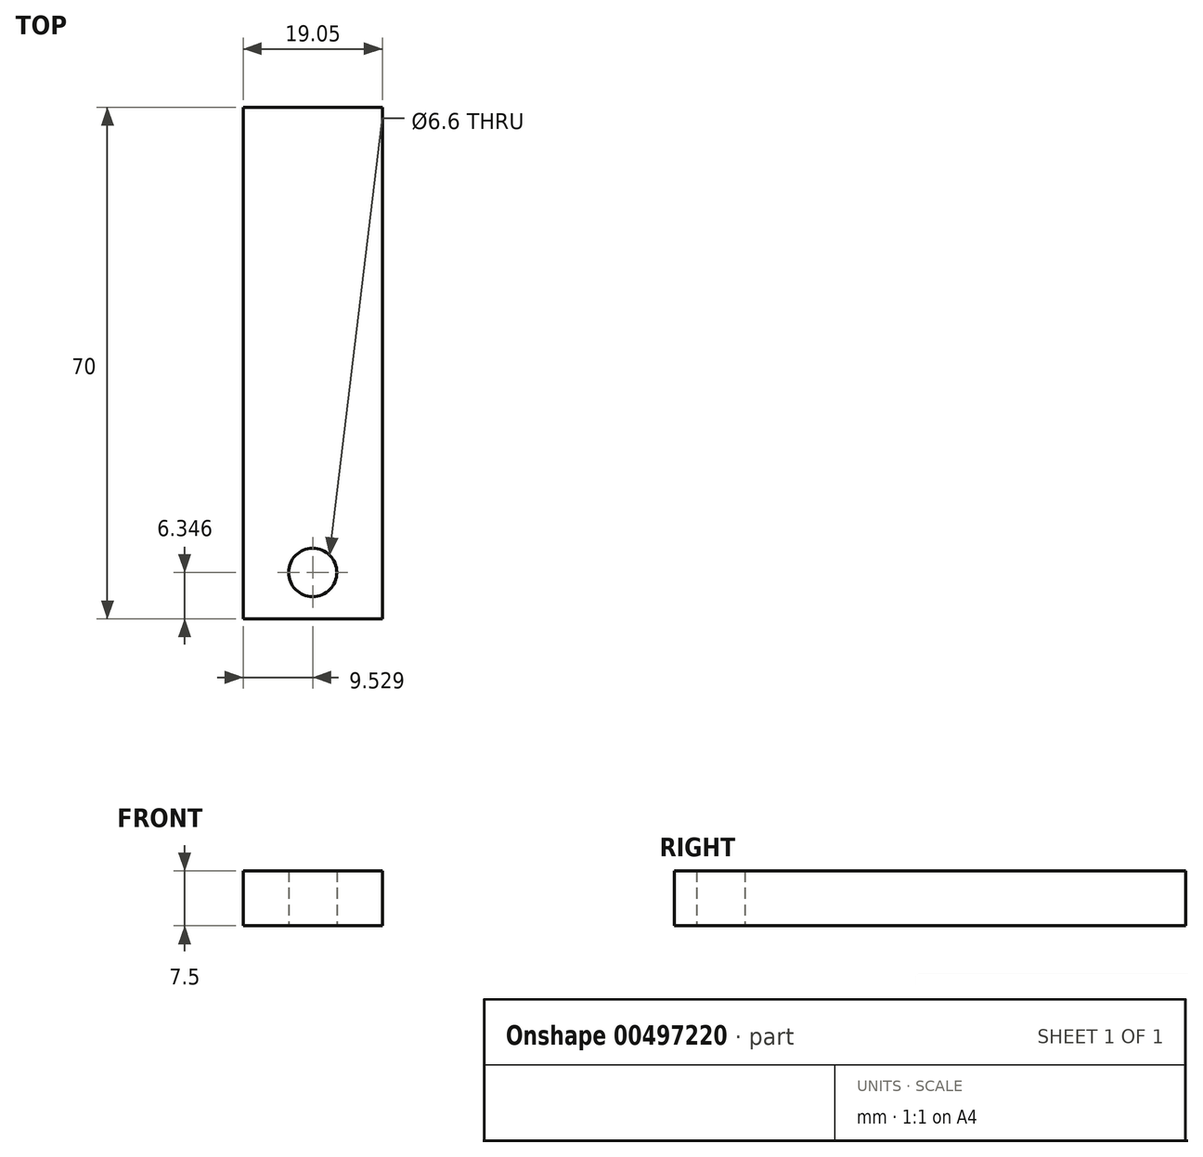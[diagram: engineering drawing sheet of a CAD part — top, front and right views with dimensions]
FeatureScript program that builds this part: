
annotation { "Feature Type Name" : "Feature", "Feature Type Description" : "" }
export const myFeature = defineFeature(function(context is Context, id is Id, definition is map)
    precondition{}
    {
        {
            var Q0;
            Q0=qCreatedBy(makeId("Top.planeOp"),FACE);
            var sketch = newSketch(context, id + "F0", { "sketchPlane" : qUnion([Q0])});
            skLineSegment(sketch, "E0.bottom", {"start": v(-12.87, 25.12) * mm, "end": v(6.18, 25.12) * mm});
            skLineSegment(sketch, "E0.top", {"start": v(-12.87, -44.88) * mm, "end": v(6.18, -44.88) * mm});
            skLineSegment(sketch, "E0.left", {"start": v(-12.87, 25.12) * mm, "end": v(-12.87, -44.88) * mm});
            skLineSegment(sketch, "E0.right", {"start": v(6.18, 25.12) * mm, "end": v(6.18, -44.88) * mm});
            skLineSegment(sketch, "E1", {"start": v(-3.34, 25.12) * mm, "end": v(-3.34, -44.88) * mm});
            skCircle(sketch, "E2", {"center": v(-3.34, -38.53) * mm, "radius": 3.3 * mm});
            skSolve(sketch);
        }
        {
            var Q0;
            {var subQ5=sQuery(id+"F0.wireOp",EDGE,"E0.left");Q0=makeQuery(id+"F0.imprint","IMPRINT",FACE,{"disambiguationData":[TD([[makeQuery(id+"F0.imprint","IMPRINT",EDGE,{"derivedFrom":subQ5}),1.0]])]});}
            var Q1;
            {var subQ0=sQuery(id+"F0.wireOp",EDGE,"E0.right");Q1=makeQuery(id+"F0.imprint","IMPRINT",FACE,{"disambiguationData":[TD([[makeQuery(id+"F0.imprint","IMPRINT",EDGE,{"derivedFrom":subQ0}),-1.0]])]});}
            extrude(context, id + "F1", {"entities" : qUnion([Q0, Q1]), "depth" : 7.5 * mm});
        }
    });
